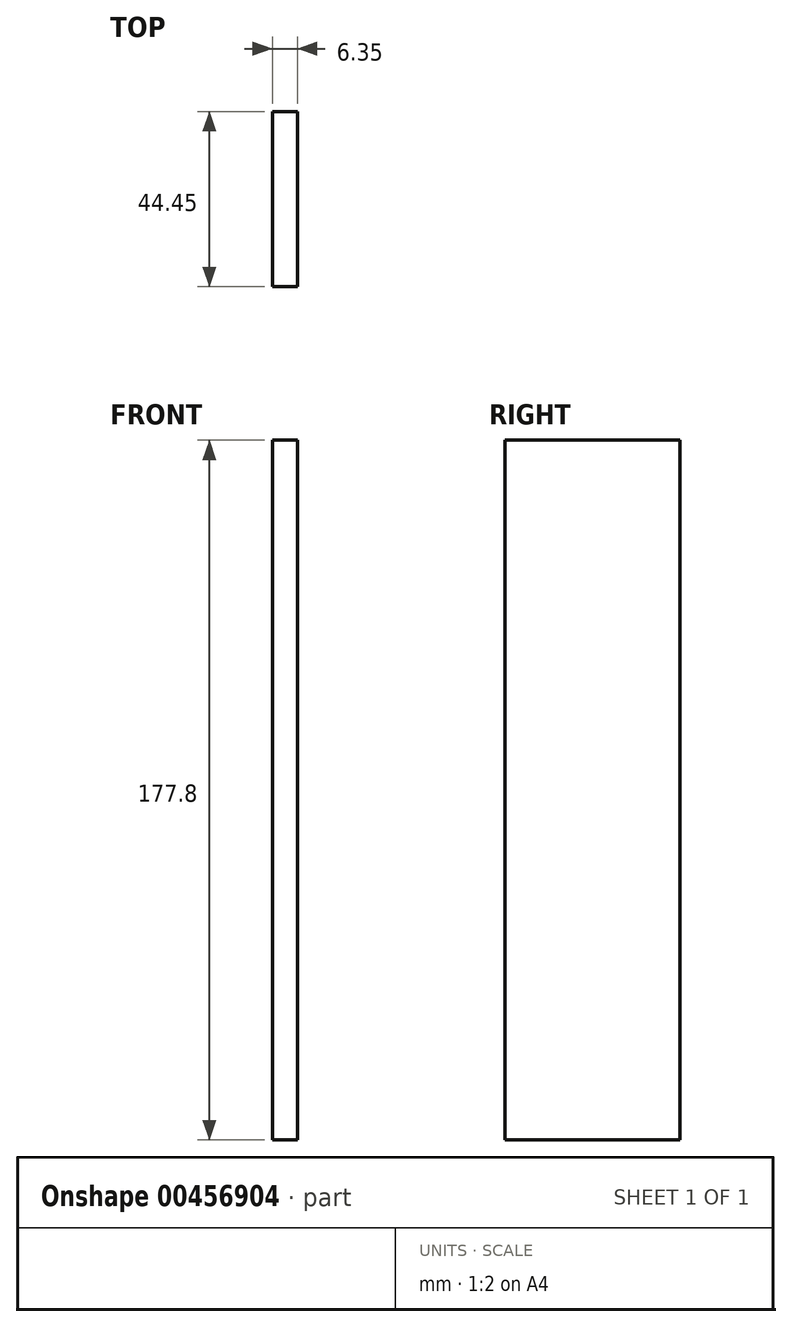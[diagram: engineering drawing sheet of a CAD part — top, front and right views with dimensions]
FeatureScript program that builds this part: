
annotation { "Feature Type Name" : "Feature", "Feature Type Description" : "" }
export const myFeature = defineFeature(function(context is Context, id is Id, definition is map)
    precondition{}
    {
        {
            var Q0;
            Q0=qCreatedBy(makeId("Right.planeOp"),FACE);
            var sketch = newSketch(context, id + "F0", { "sketchPlane" : qUnion([Q0])});
            skLineSegment(sketch, "E0.bottom", {"start": v(-94.16, 67.8) * mm, "end": v(-49.7, 67.8) * mm});
            skLineSegment(sketch, "E0.top", {"start": v(-94.16, -110) * mm, "end": v(-49.7, -110) * mm});
            skLineSegment(sketch, "E0.left", {"start": v(-94.16, 67.8) * mm, "end": v(-94.16, -110) * mm});
            skLineSegment(sketch, "E1", {"start": v(-49.7, -110) * mm, "end": v(-49.7, 67.8) * mm});
            skSolve(sketch);
        }
        {
            var Q0;
            Q0=makeQuery(id+"F0.imprint","IMPRINT",FACE,{"disambiguationData":[TD([[makeQuery(id+"F0.imprint","IMPRINT",EDGE,{"derivedFrom":sQuery(id+"F0.wireOp",EDGE,"E0.bottom")}),-1.0]])]});
            extrude(context, id + "F1", {"entities" : qUnion([Q0]), "depth" : 6.35 * mm});
        }
    });
